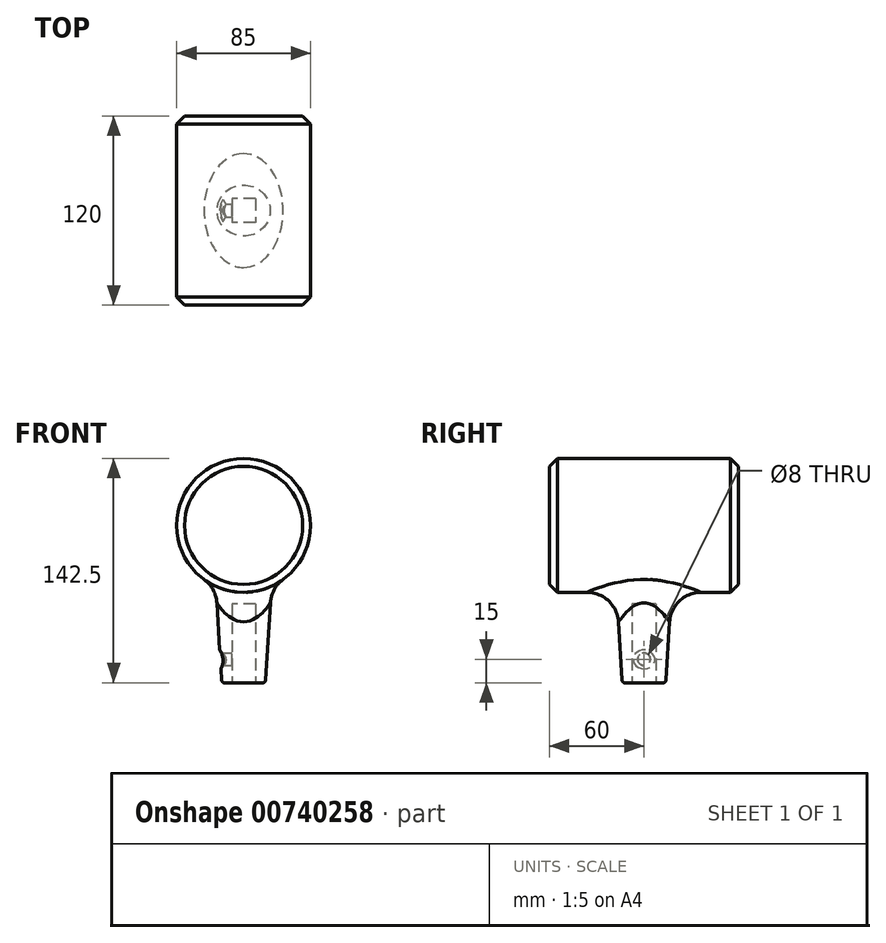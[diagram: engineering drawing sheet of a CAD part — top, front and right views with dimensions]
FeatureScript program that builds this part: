
annotation { "Feature Type Name" : "Feature", "Feature Type Description" : "" }
export const myFeature = defineFeature(function(context is Context, id is Id, definition is map)
    precondition{}
    {
        {
            var Q0;
            Q0=qCreatedBy(makeId("Front.planeOp"),FACE);
            var sketch = newSketch(context, id + "F0", { "sketchPlane" : qUnion([Q0])});
            skCircle(sketch, "E0", {"center": v(0, 0) * mm, "radius": 42.5 * mm});
            skSolve(sketch);
        }
        {
            var Q0;
            Q0=makeQuery(id+"F0.imprint","IMPRINT",FACE,{"disambiguationData":[TD([[makeQuery(id+"F0.imprint","IMPRINT",EDGE,{"derivedFrom":sQuery(id+"F0.wireOp",EDGE,"E0")}),1.0]])]});
            var Q1;
            Q1=sQuery(id+"F0.wireOp",EDGE,"E0");
            extrude(context, id + "F1", {"entities" : qUnion([Q0]), "surfaceEntities" : qUnion([Q1]), "endBound" : BoundingType.SYMMETRIC, "oppositeDirection" : true, "depth" : 120 * mm, "offsetDistance" : 25 * mm});
        }
        {
            var Q0;
            Q0=qCreatedBy(makeId("Top.planeOp"),FACE);
            var sketch = newSketch(context, id + "F2", { "sketchPlane" : qUnion([Q0])});
            skCircle(sketch, "E1", {"center": v(0, 0) * mm, "radius": 20 * mm});
            skSolve(sketch);
        }
        {
            var Q0;
            Q0=qSketchRegion(id+"F2",true);
            extrude(context, id + "F3", {"entities" : qUnion([Q0]), "operationType" : NewBodyOperationType.ADD, "oppositeDirection" : true, "depth" : 100 * mm, "offsetDistance" : 25 * mm, "hasDraft" : true, "draftAngle" : 3.5 * degree, "draftPullDirection" : true});
        }
        {
            var Q0;
            Q0=makeQuery(id+"F3.opExtrude","CAP_FACE",FACE,{"disambiguationData":[OSD([sQuery(id+"F2.wireOp",EDGE,"E1")])],"isStart":false});
            var sketch = newSketch(context, id + "F4", { "sketchPlane" : qUnion([Q0])});
            skLineSegment(sketch, "E2.bottom", {"start": v(7.5, -7.5) * mm, "end": v(-7.5, -7.5) * mm});
            skLineSegment(sketch, "E2.top", {"start": v(7.5, 7.5) * mm, "end": v(-7.5, 7.5) * mm});
            skLineSegment(sketch, "E2.left", {"start": v(7.5, -7.5) * mm, "end": v(7.5, 7.5) * mm});
            skLineSegment(sketch, "E2.right", {"start": v(-7.5, -7.5) * mm, "end": v(-7.5, 7.5) * mm});
            skPoint(sketch, "E2.middle", {"position": v(0, 0) * mm});
            skSolve(sketch);
        }
        {
            var Q0;
            Q0=qSketchRegion(id+"F4",true);
            extrude(context, id + "F5", {"entities" : qUnion([Q0]), "operationType" : NewBodyOperationType.REMOVE, "oppositeDirection" : true, "depth" : 50 * mm, "offsetDistance" : 25 * mm});
        }
        {
            var Q0;
            Q0=qCreatedBy(makeId("Right.planeOp"),FACE);
            var sketch = newSketch(context, id + "F6", { "sketchPlane" : qUnion([Q0])});
            skCircle(sketch, "E3", {"center": v(0, -85) * mm, "radius": 4 * mm});
            skSolve(sketch);
        }
        {
            var Q0;
            Q0=qSketchRegion(id+"F6",true);
            extrude(context, id + "F7", {"entities" : qUnion([Q0]), "operationType" : NewBodyOperationType.REMOVE, "oppositeDirection" : true, "depth" : 50 * mm, "offsetDistance" : 25 * mm});
        }
        {
            var Q0;
            Q0=makeQuery(id+"F1.opExtrude","CAP_FACE",FACE,{"disambiguationData":[OSD([sQuery(id+"F0.wireOp",EDGE,"E0")])],"isStart":false});
            var Q1;
            Q1=makeQuery(id+"F1.opExtrude","CAP_FACE",FACE,{"disambiguationData":[OSD([sQuery(id+"F0.wireOp",EDGE,"E0")])],"isStart":true});
            chamfer(context, id + "F8", {"entities" : qUnion([Q0, Q1]), "width" : 5 * mm, "tangentPropagation" : true});
        }
        {
            var Q0;
            Q0=makeQuery(id+"F3.boolean.opBoolean","INTERSECT",EDGE,{"derivedFrom":[makeQuery(id+"F1.opExtrude","SWEPT_FACE",FACE,{"disambiguationData":[OSD([sQuery(id+"F0.wireOp",EDGE,"E0")])]}),makeQuery(id+"F3.opExtrude","SWEPT_FACE",FACE,{"disambiguationData":[OSD([sQuery(id+"F2.wireOp",EDGE,"E1")])]})]});
            fillet(context, id + "F9", {"entities" : qUnion([Q0]), "radius" : 20 * mm, "tangentPropagation" : true, "allowEdgeOverflow" : false});
        }
        {
            var Q0;
            Q0=makeQuery(id+"F3.opExtrude","CAP_EDGE",EDGE,{"disambiguationData":[OSD([sQuery(id+"F2.wireOp",EDGE,"E1")])],"isStart":false});
            fillet(context, id + "F10", {"entities" : qUnion([Q0]), "radius" : 2 * mm, "tangentPropagation" : true, "allowEdgeOverflow" : false});
        }
        {
            var Q0;
            Q0=makeQuery(id+"F7.boolean.opBoolean","INTERSECT",EDGE,{"derivedFrom":[makeQuery(id+"F3.opExtrude","SWEPT_FACE",FACE,{"disambiguationData":[OSD([sQuery(id+"F2.wireOp",EDGE,"E1")])]}),makeQuery(id+"F7.opExtrude","SWEPT_FACE",FACE,{"disambiguationData":[OSD([sQuery(id+"F6.wireOp",EDGE,"E3")])]})]});
            chamfer(context, id + "F11", {"entities" : qUnion([Q0]), "width" : 2 * mm, "tangentPropagation" : true});
        }
    });
